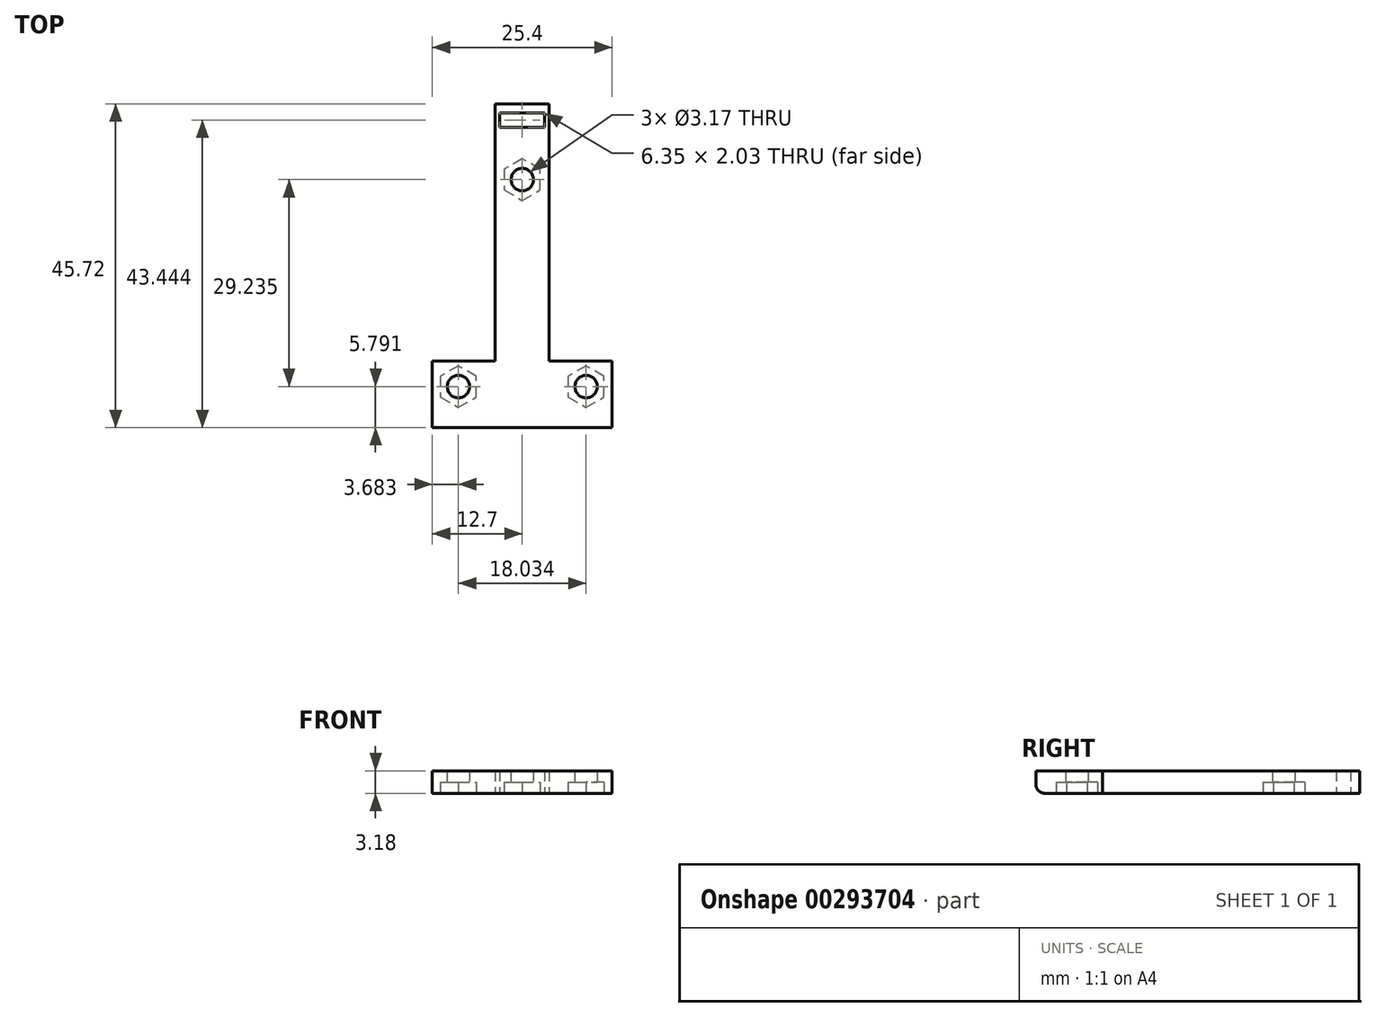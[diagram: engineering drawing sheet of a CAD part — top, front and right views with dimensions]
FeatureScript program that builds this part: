
annotation { "Feature Type Name" : "Feature", "Feature Type Description" : "" }
export const myFeature = defineFeature(function(context is Context, id is Id, definition is map)
    precondition{}
    {
        {
            var Q0;
            Q0=qCreatedBy(makeId("Top.planeOp"),FACE);
            var sketch = newSketch(context, id + "F0", { "sketchPlane" : qUnion([Q0])});
            skPoint(sketch, "E0.middle", {"position": v(0, 0) * mm});
            skCircle(sketch, "E1", {"center": v(9.02, -17.07) * mm, "radius": 1.59 * mm});
            skCircle(sketch, "E2", {"center": v(0, 12.17) * mm, "radius": 1.59 * mm});
            skLineSegment(sketch, "E3", {"start": v(0, 22.86) * mm, "end": v(3.8, 22.86) * mm});
            skLineSegment(sketch, "E4", {"start": v(3.8, 22.86) * mm, "end": v(3.81, -13.46) * mm});
            skLineSegment(sketch, "E5", {"start": v(3.81, -13.46) * mm, "end": v(12.7, -13.46) * mm});
            skLineSegment(sketch, "E6", {"start": v(12.7, -13.46) * mm, "end": v(12.7, -22.86) * mm});
            skLineSegment(sketch, "E7", {"start": v(12.7, -22.86) * mm, "end": v(0, -22.86) * mm});
            skLineSegment(sketch, "E8", {"start": v(0, -22.86) * mm, "end": v(0, 22.86) * mm});
            skLineSegment(sketch, "E9.MirrorCS", {"start": v(0, 22.86) * mm, "end": v(-3.81, 22.86) * mm});
            skLineSegment(sketch, "E10.MirrorCS", {"start": v(-3.8, 22.86) * mm, "end": v(-3.81, -13.46) * mm});
            skLineSegment(sketch, "E11.MirrorCS", {"start": v(-3.8, -13.46) * mm, "end": v(-12.7, -13.46) * mm});
            skLineSegment(sketch, "E12.MirrorCS", {"start": v(-12.7, -13.46) * mm, "end": v(-12.7, -22.86) * mm});
            skCircle(sketch, "E13.MirrorC", {"center": v(-9.02, -17.07) * mm, "radius": 1.59 * mm});
            skLineSegment(sketch, "E14.MirrorCS", {"start": v(-12.7, -22.86) * mm, "end": v(0, -22.86) * mm});
            skLineSegment(sketch, "E15.bottom", {"start": v(-3.18, 19.57) * mm, "end": v(3.18, 19.57) * mm});
            skLineSegment(sketch, "E15.top", {"start": v(-3.18, 21.6) * mm, "end": v(3.17, 21.6) * mm});
            skLineSegment(sketch, "E15.left", {"start": v(-3.18, 19.57) * mm, "end": v(-3.18, 21.6) * mm});
            skLineSegment(sketch, "E15.right", {"start": v(3.18, 19.57) * mm, "end": v(3.18, 21.6) * mm});
            skPoint(sketch, "E15.middle", {"position": v(0, 20.58) * mm});
            skSolve(sketch);
        }
        {
            var Q0;
            Q0 = qSketchRegion(id + "F0", true);
            extrude(context, id + "F1", {"entities" : qUnion([Q0]), "depth" : 3.17 * mm});
        }
        {
            var Q0;
            Q0=makeQuery(id+"F1.opExtrude","CAP_EDGE",EDGE,{"disambiguationData":[OSD([sQuery(id+"F0.wireOp",EDGE,"E7"),sQuery(id+"F0.wireOp",EDGE,"E14.MirrorCS")])],"isStart":true});
            fillet(context, id + "F2", {"entities" : qUnion([Q0]), "radius" : 1.27 * mm, "tangentPropagation" : true, "allowEdgeOverflow" : false});
        }
        {
            var Q0;
            Q0=makeQuery(id+"F1.opExtrude","CAP_FACE",FACE,{"disambiguationData":[OSD([sQuery(id+"F0.wireOp",EDGE,"E1"),sQuery(id+"F0.wireOp",EDGE,"E2"),sQuery(id+"F0.wireOp",EDGE,"E3"),sQuery(id+"F0.wireOp",EDGE,"E4"),sQuery(id+"F0.wireOp",EDGE,"E5"),sQuery(id+"F0.wireOp",EDGE,"E6"),sQuery(id+"F0.wireOp",EDGE,"E7"),sQuery(id+"F0.wireOp",EDGE,"E9.MirrorCS"),sQuery(id+"F0.wireOp",EDGE,"E10.MirrorCS"),sQuery(id+"F0.wireOp",EDGE,"E11.MirrorCS"),sQuery(id+"F0.wireOp",EDGE,"E12.MirrorCS"),sQuery(id+"F0.wireOp",EDGE,"E13.MirrorC"),sQuery(id+"F0.wireOp",EDGE,"E14.MirrorCS")])],"isStart":true});
            var sketch = newSketch(context, id + "F3", { "sketchPlane" : qUnion([Q0])});
            skCircle(sketch, "E16.cCircle", {"center": v(-9.02, 17.07) * mm, "radius": 2.54 * mm, "construction": true});
            skLineSegment(sketch, "E16.0", {"start": v(-9.02, 20) * mm, "end": v(-6.48, 18.54) * mm});
            skLineSegment(sketch, "E16.1", {"start": v(-6.48, 18.54) * mm, "end": v(-6.48, 15.6) * mm});
            skLineSegment(sketch, "E16.2", {"start": v(-6.48, 15.6) * mm, "end": v(-9.02, 14.14) * mm});
            skLineSegment(sketch, "E16.3", {"start": v(-9.02, 14.14) * mm, "end": v(-11.56, 15.6) * mm});
            skLineSegment(sketch, "E16.4", {"start": v(-11.56, 15.6) * mm, "end": v(-11.56, 18.54) * mm});
            skLineSegment(sketch, "E16.5", {"start": v(-11.56, 18.54) * mm, "end": v(-9.02, 20) * mm});
            skPoint(sketch, "E16.0.midPoint", {"position": v(-7.75, 19.27) * mm});
            skCircle(sketch, "E17.cCircle", {"center": v(9.02, 17.07) * mm, "radius": 2.54 * mm, "construction": true});
            skLineSegment(sketch, "E17.0", {"start": v(6.48, 18.54) * mm, "end": v(9.02, 20) * mm});
            skLineSegment(sketch, "E17.1", {"start": v(9.02, 20) * mm, "end": v(11.56, 18.54) * mm});
            skLineSegment(sketch, "E17.2", {"start": v(11.56, 18.54) * mm, "end": v(11.56, 15.6) * mm});
            skLineSegment(sketch, "E17.3", {"start": v(11.56, 15.6) * mm, "end": v(9.02, 14.14) * mm});
            skLineSegment(sketch, "E17.4", {"start": v(9.02, 14.14) * mm, "end": v(6.48, 15.6) * mm});
            skLineSegment(sketch, "E17.5", {"start": v(6.48, 15.6) * mm, "end": v(6.48, 18.54) * mm});
            skPoint(sketch, "E17.0.midPoint", {"position": v(7.75, 19.27) * mm});
            skCircle(sketch, "E18.cCircle", {"center": v(0, -12.17) * mm, "radius": 2.54 * mm, "construction": true});
            skLineSegment(sketch, "E18.0", {"start": v(0, -9.23) * mm, "end": v(2.54, -10.7) * mm});
            skLineSegment(sketch, "E18.1", {"start": v(2.54, -10.7) * mm, "end": v(2.54, -13.63) * mm});
            skLineSegment(sketch, "E18.2", {"start": v(2.54, -13.63) * mm, "end": v(0, -15.1) * mm});
            skLineSegment(sketch, "E18.3", {"start": v(0, -15.1) * mm, "end": v(-2.54, -13.63) * mm});
            skLineSegment(sketch, "E18.4", {"start": v(-2.54, -13.63) * mm, "end": v(-2.54, -10.7) * mm});
            skLineSegment(sketch, "E18.5", {"start": v(-2.54, -10.7) * mm, "end": v(0, -9.23) * mm});
            skPoint(sketch, "E18.0.midPoint", {"position": v(1.27, -9.97) * mm});
            skSolve(sketch);
        }
        {
            var Q0;
            Q0 = qSketchRegion(id + "F3", true);
            extrude(context, id + "F4", {"entities" : qUnion([Q0]), "operationType" : NewBodyOperationType.REMOVE, "oppositeDirection" : true, "depth" : 1.59 * mm});
        }
    });
